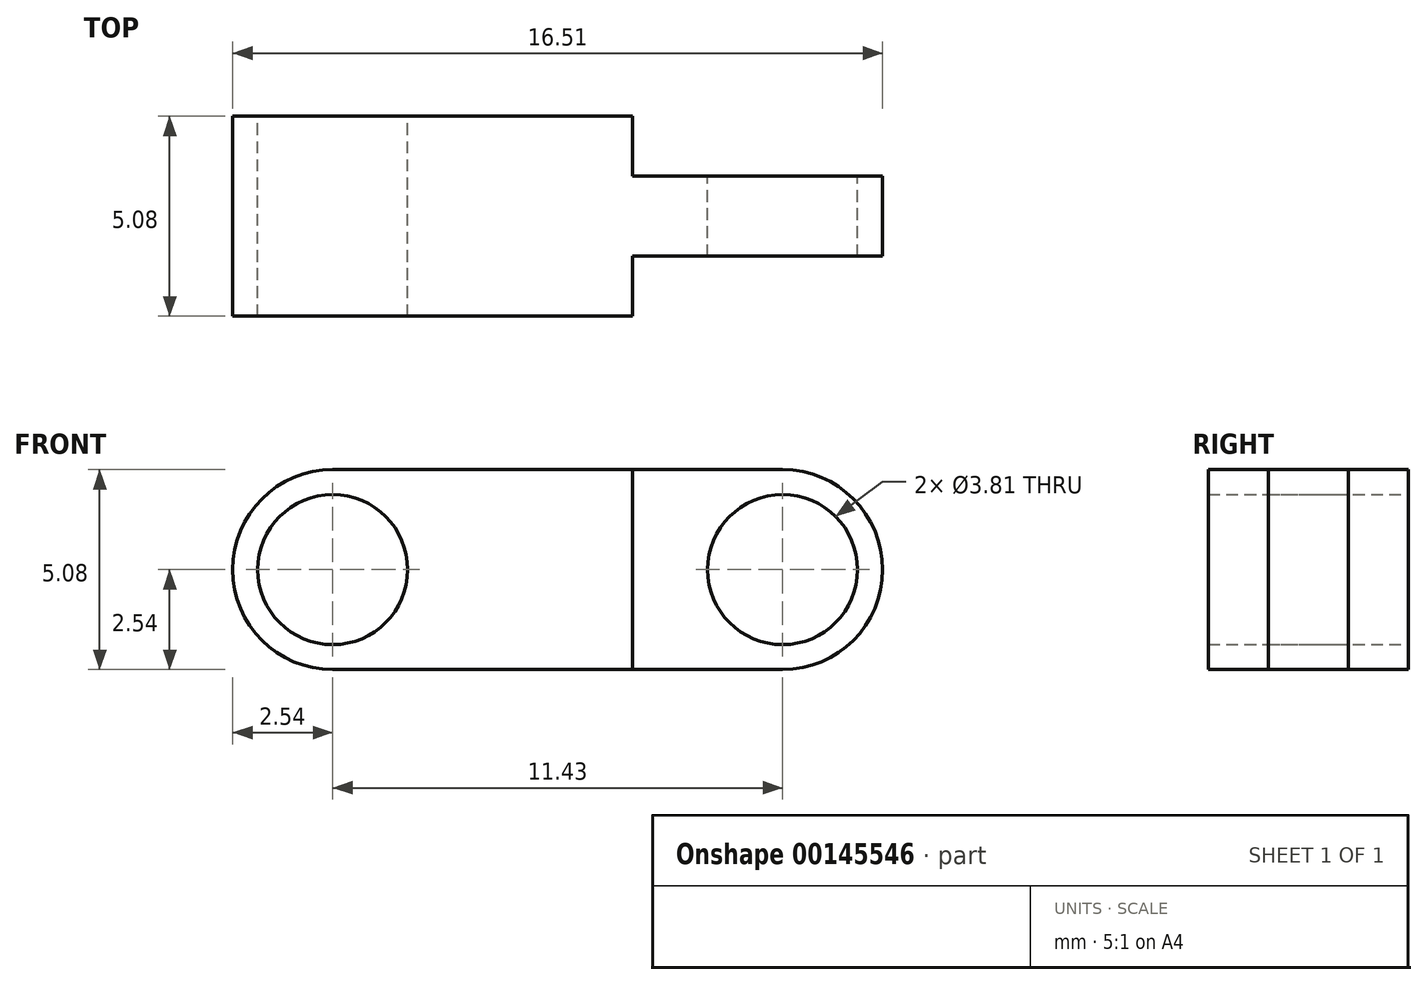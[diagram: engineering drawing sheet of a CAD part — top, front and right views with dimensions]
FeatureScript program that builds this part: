
annotation { "Feature Type Name" : "Feature", "Feature Type Description" : "" }
export const myFeature = defineFeature(function(context is Context, id is Id, definition is map)
    precondition{}
    {
        {
            var Q0;
            Q0=qCreatedBy(makeId("Top.planeOp"),FACE);
            var sketch = newSketch(context, id + "F0", { "sketchPlane" : qUnion([Q0])});
            skLineSegment(sketch, "E0.bottom", {"start": v(0, 0) * mm, "end": v(10.16, 0) * mm});
            skLineSegment(sketch, "E0.top", {"start": v(0, -5.08) * mm, "end": v(16.51, -5.08) * mm});
            skLineSegment(sketch, "E0.left", {"start": v(0, 0) * mm, "end": v(0, -5.08) * mm});
            skLineSegment(sketch, "E0.right", {"start": v(16.51, -1.52) * mm, "end": v(16.51, -5.08) * mm});
            skLineSegment(sketch, "E1", {"start": v(10.16, 0) * mm, "end": v(10.16, -1.52) * mm});
            skLineSegment(sketch, "E2", {"start": v(10.16, -1.52) * mm, "end": v(16.51, -1.52) * mm});
            skPoint(sketch, "E3.orphan", {"position": v(16.51, 0) * mm});
            skLineSegment(sketch, "E4", {"start": v(10.16, -5.08) * mm, "end": v(10.16, -3.56) * mm});
            skLineSegment(sketch, "E5", {"start": v(10.16, -3.56) * mm, "end": v(16.51, -3.56) * mm});
            skSolve(sketch);
        }
        {
            var Q0;
            Q0=makeQuery(id+"F0.imprint","IMPRINT",FACE,{"disambiguationData":[TD([[makeQuery(id+"F0.imprint","IMPRINT",EDGE,{"derivedFrom":sQuery(id+"F0.wireOp",EDGE,"E0.bottom")}),-1.0]])]});
            extrude(context, id + "F1", {"entities" : qUnion([Q0]), "depth" : 5.08 * mm});
        }
        {
            var Q0;
            Q0=makeQuery(id+"F1.opExtrude","CAP_EDGE",EDGE,{"disambiguationData":[OSD([sQuery(id+"F0.wireOp",EDGE,"E0.right")])],"isStart":false});
            var Q1;
            Q1=makeQuery(id+"F1.opExtrude","CAP_EDGE",EDGE,{"disambiguationData":[OSD([sQuery(id+"F0.wireOp",EDGE,"E0.right")])],"isStart":true});
            var Q2;
            Q2=makeQuery(id+"F1.opExtrude","CAP_EDGE",EDGE,{"disambiguationData":[OSD([sQuery(id+"F0.wireOp",EDGE,"E0.left")])],"isStart":false});
            var Q3;
            Q3=makeQuery(id+"F1.opExtrude","CAP_EDGE",EDGE,{"disambiguationData":[OSD([sQuery(id+"F0.wireOp",EDGE,"E0.left")])],"isStart":true});
            fillet(context, id + "F2", {"entities" : qUnion([Q0, Q1, Q2, Q3]), "radius" : 2.54 * mm, "tangentPropagation" : true, "allowEdgeOverflow" : false});
        }
        {
            var Q0;
            Q0=makeQuery(id+"F1.opExtrude","SWEPT_FACE",FACE,{"disambiguationData":[OSD([sQuery(id+"F0.wireOp",EDGE,"E2")])]});
            var sketch = newSketch(context, id + "F3", { "sketchPlane" : qUnion([Q0])});
            skCircle(sketch, "E6", {"center": v(-13.97, 2.54) * mm, "radius": 1.9 * mm});
            skSolve(sketch);
        }
        {
            var Q0;
            Q0=makeQuery(id+"F3.imprint","IMPRINT",FACE,{"disambiguationData":[TD([[makeQuery(id+"F3.imprint","IMPRINT",EDGE,{"derivedFrom":sQuery(id+"F3.wireOp",EDGE,"E6")}),1.0]])]});
            extrude(context, id + "F4", {"entities" : qUnion([Q0]), "operationType" : NewBodyOperationType.REMOVE, "oppositeDirection" : true, "depth" : 25.4 * mm});
        }
        {
            var Q0;
            Q0=makeQuery(id+"F1.opExtrude","SWEPT_FACE",FACE,{"disambiguationData":[OSD([sQuery(id+"F0.wireOp",EDGE,"E0.bottom")])]});
            var sketch = newSketch(context, id + "F5", { "sketchPlane" : qUnion([Q0])});
            skCircle(sketch, "E7", {"center": v(-2.54, 2.54) * mm, "radius": 1.9 * mm});
            skPoint(sketch, "E8", {"position": v(0, 2.54) * mm});
            skArc(sketch, "E9.0", {"start": v(-13.97, 5.08) * mm, "mid": v(-16.51, 2.54) * mm, "end": v(-13.97, 0) * mm});
            skPoint(sketch, "E10", {"position": v(-16.51, 2.54) * mm});
            skSolve(sketch);
        }
        {
            var Q0;
            Q0=makeQuery(id+"F5.imprint","IMPRINT",FACE,{"disambiguationData":[TD([[makeQuery(id+"F5.imprint","IMPRINT",EDGE,{"derivedFrom":sQuery(id+"F5.wireOp",EDGE,"E7")}),1.0]])]});
            extrude(context, id + "F6", {"entities" : qUnion([Q0]), "operationType" : NewBodyOperationType.REMOVE, "oppositeDirection" : true, "depth" : 5.08 * mm});
        }
    });
